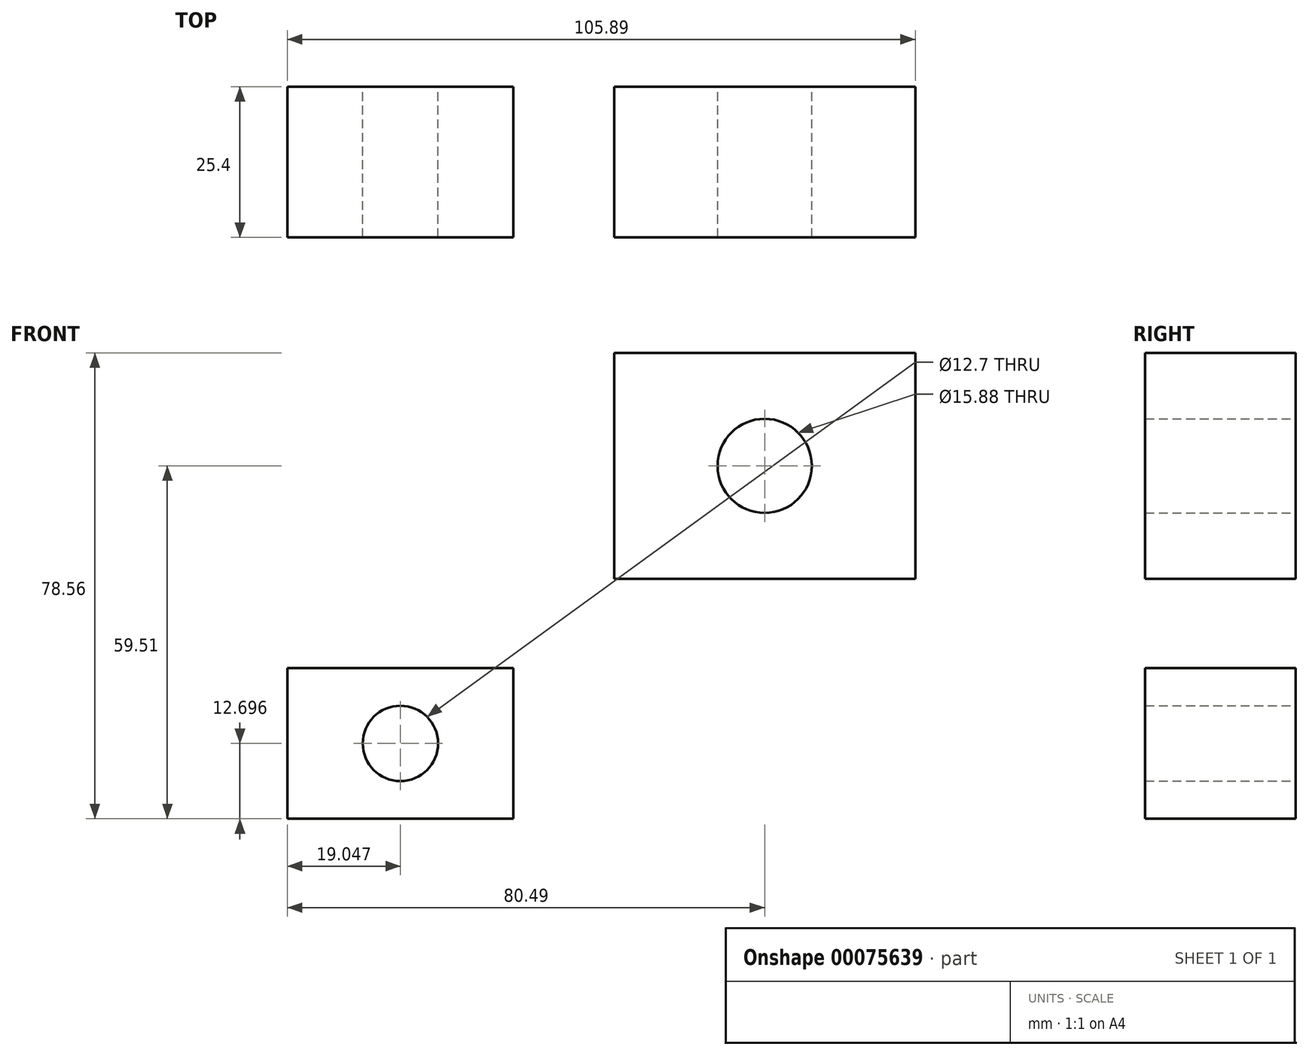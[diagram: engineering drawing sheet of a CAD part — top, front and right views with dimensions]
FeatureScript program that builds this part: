
annotation { "Feature Type Name" : "Feature", "Feature Type Description" : "" }
export const myFeature = defineFeature(function(context is Context, id is Id, definition is map)
    precondition{}
    {
        {
            var Q0;
            Q0=qCreatedBy(makeId("Front.planeOp"),FACE);
            var sketch = newSketch(context, id + "F0", { "sketchPlane" : qUnion([Q0])});
            skLineSegment(sketch, "E0.bottom", {"start": v(0, 0) * mm, "end": v(50.8, 0) * mm});
            skLineSegment(sketch, "E0.top", {"start": v(0, 38.1) * mm, "end": v(50.8, 38.1) * mm});
            skLineSegment(sketch, "E0.left", {"start": v(0, 0) * mm, "end": v(0, 38.1) * mm});
            skLineSegment(sketch, "E0.right", {"start": v(50.8, 0) * mm, "end": v(50.8, 38.1) * mm});
            skPoint(sketch, "E1", {"position": v(25.4, 19.05) * mm});
            skCircle(sketch, "E2", {"center": v(25.4, 19.05) * mm, "radius": 7.94 * mm});
            skSolve(sketch);
        }
        {
            var Q0;
            Q0=makeQuery(id+"F0.imprint","IMPRINT",FACE,{"disambiguationData":[TD([[makeQuery(id+"F0.imprint","IMPRINT",EDGE,{"derivedFrom":sQuery(id+"F0.wireOp",EDGE,"E0.bottom")}),1.0]])]});
            extrude(context, id + "F1", {"entities" : qUnion([Q0]), "depth" : 25.4 * mm});
        }
        {
            var Q0;
            Q0=qCreatedBy(makeId("Front.planeOp"),FACE);
            var sketch = newSketch(context, id + "F2", { "sketchPlane" : qUnion([Q0])});
            skLineSegment(sketch, "E3.bottom", {"start": v(-17, -15.06) * mm, "end": v(-55.1, -15.06) * mm});
            skLineSegment(sketch, "E3.top", {"start": v(-17, -40.46) * mm, "end": v(-55.1, -40.46) * mm});
            skLineSegment(sketch, "E3.left", {"start": v(-17, -15.06) * mm, "end": v(-17, -40.46) * mm});
            skLineSegment(sketch, "E3.right", {"start": v(-55.1, -15.06) * mm, "end": v(-55.1, -40.46) * mm});
            skCircle(sketch, "E4", {"center": v(-36.04, -27.76) * mm, "radius": 6.35 * mm});
            skPoint(sketch, "E4.centerSnap0", {"position": v(-36.04, -15.06) * mm});
            skPoint(sketch, "E4.centerSnap1", {"position": v(-55.1, -27.76) * mm});
            skSolve(sketch);
        }
        {
            var Q0;
            Q0=makeQuery(id+"F2.imprint","IMPRINT",FACE,{"disambiguationData":[TD([[makeQuery(id+"F2.imprint","IMPRINT",EDGE,{"derivedFrom":sQuery(id+"F2.wireOp",EDGE,"E3.bottom")}),1.0]])]});
            extrude(context, id + "F3", {"entities" : qUnion([Q0]), "depth" : 25.4 * mm});
        }
    });
